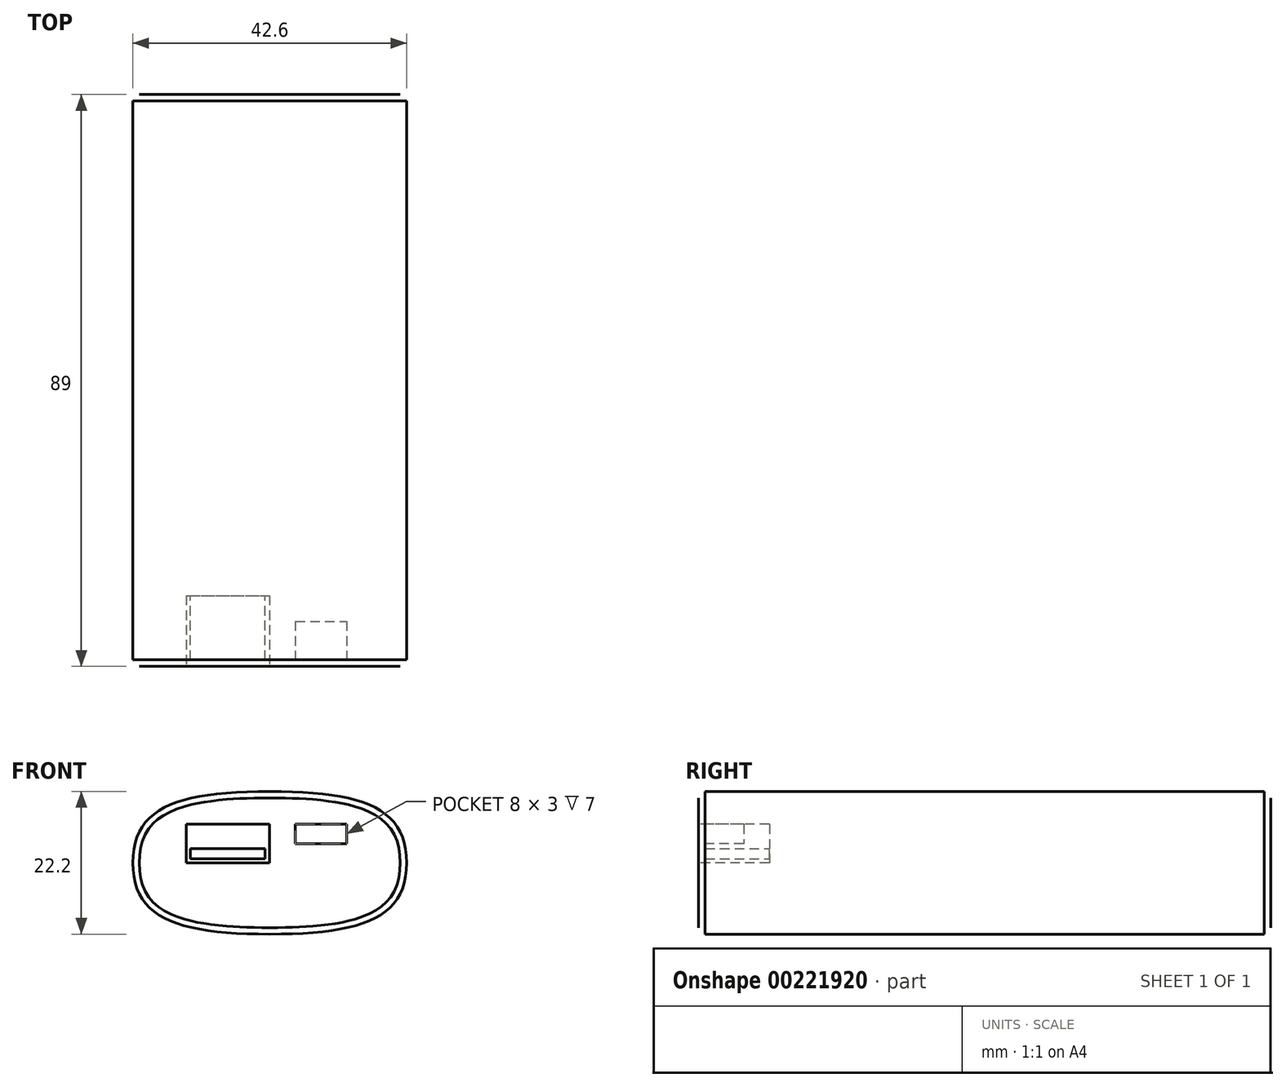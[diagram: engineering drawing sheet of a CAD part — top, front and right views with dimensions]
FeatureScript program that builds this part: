
annotation { "Feature Type Name" : "Feature", "Feature Type Description" : "" }
export const myFeature = defineFeature(function(context is Context, id is Id, definition is map)
    precondition{}
    {
        {
            var Q0;
            Q0=qCreatedBy(makeId("Front.planeOp"),FACE);
            var sketch = newSketch(context, id + "F0", { "sketchPlane" : qUnion([Q0])});
            skLineSegment(sketch, "E0", {"start": v(0, 11.1) * mm, "end": v(0, -11.1) * mm, "construction": true});
            skLineSegment(sketch, "E1", {"start": v(-21.3, 0) * mm, "end": v(21.3, 0) * mm, "construction": true});
            skFitSpline(sketch, "E2", {"points": [v(0, 11.1) * mm, v(-21.3, 0) * mm], "startDerivative": vector(-42.35, 0) * mm, "endDerivative": vector(0, -26.2) * mm});
            skFitSpline(sketch, "E3.MirrorCS", {"points": [v(0, -11.1) * mm, v(-21.3, 0) * mm], "startDerivative": vector(-42.35, 0) * mm, "endDerivative": vector(0, 26.2) * mm});
            skFitSpline(sketch, "E4.MirrorCS", {"points": [v(0, 11.1) * mm, v(21.3, 0) * mm], "startDerivative": vector(42.35, 0) * mm, "endDerivative": vector(0, -26.2) * mm});
            skFitSpline(sketch, "E5.MirrorCS", {"points": [v(0, -11.1) * mm, v(21.3, 0) * mm], "startDerivative": vector(42.35, 0) * mm, "endDerivative": vector(0, 26.2) * mm});
            skSolve(sketch);
        }
        {
            var Q0;
            Q0=makeQuery(id+"F0.imprint","IMPRINT",FACE,{"disambiguationData":[TD([[makeQuery(id+"F0.imprint","IMPRINT",EDGE,{"derivedFrom":sQuery(id+"F0.wireOp",EDGE,"E2")}),1.0]])]});
            extrude(context, id + "F1", {"entities" : qUnion([Q0]), "depth" : 89 * mm});
        }
        {
            var Q0;
            Q0=makeQuery(id+"F1.opExtrude","CAP_FACE",FACE,{"disambiguationData":[OSD([sQuery(id+"F0.wireOp",EDGE,"E2"),sQuery(id+"F0.wireOp",EDGE,"E3.MirrorCS"),sQuery(id+"F0.wireOp",EDGE,"E4.MirrorCS"),sQuery(id+"F0.wireOp",EDGE,"E5.MirrorCS")])],"isStart":false});
            var sketch = newSketch(context, id + "F2", { "sketchPlane" : qUnion([Q0])});
            skLineSegment(sketch, "E6.bottom", {"start": v(-13, 6) * mm, "end": v(0, 6) * mm});
            skLineSegment(sketch, "E6.top", {"start": v(-13, 0) * mm, "end": v(0, 0) * mm});
            skLineSegment(sketch, "E6.left", {"start": v(-13, 6) * mm, "end": v(-13, 0) * mm});
            skLineSegment(sketch, "E6.right", {"start": v(0, 6) * mm, "end": v(0, 0) * mm});
            skPoint(sketch, "E7.firstSnap0", {"position": v(-6.5, 6) * mm});
            skLineSegment(sketch, "E7.bottom", {"start": v(4, 6) * mm, "end": v(12, 6) * mm});
            skLineSegment(sketch, "E7.top", {"start": v(4, 3) * mm, "end": v(12, 3) * mm});
            skLineSegment(sketch, "E7.left", {"start": v(4, 6) * mm, "end": v(4, 3) * mm});
            skLineSegment(sketch, "E7.right", {"start": v(12, 6) * mm, "end": v(12, 3) * mm});
            skSolve(sketch);
        }
        {
            var Q0;
            Q0=makeQuery(id+"F2.imprint","IMPRINT",FACE,{"disambiguationData":[TD([[makeQuery(id+"F2.imprint","IMPRINT",EDGE,{"derivedFrom":sQuery(id+"F2.wireOp",EDGE,"E6.bottom")}),-1.0]])]});
            extrude(context, id + "F3", {"entities" : qUnion([Q0]), "operationType" : NewBodyOperationType.REMOVE, "oppositeDirection" : true, "depth" : 11 * mm});
        }
        {
            var Q0;
            Q0=makeQuery(id+"F2.imprint","IMPRINT",FACE,{"disambiguationData":[TD([[makeQuery(id+"F2.imprint","IMPRINT",EDGE,{"derivedFrom":sQuery(id+"F2.wireOp",EDGE,"E7.bottom")}),-1.0]])]});
            extrude(context, id + "F4", {"entities" : qUnion([Q0]), "operationType" : NewBodyOperationType.REMOVE, "oppositeDirection" : true, "depth" : 7 * mm});
        }
        {
            var Q0;
            Q0=makeQuery(id+"F1.opExtrude","CAP_EDGE",EDGE,{"disambiguationData":[OSD([sQuery(id+"F0.wireOp",EDGE,"E2")])],"isStart":false});
            var Q1;
            Q1=makeQuery(id+"F1.opExtrude","CAP_EDGE",EDGE,{"disambiguationData":[OSD([sQuery(id+"F0.wireOp",EDGE,"E2")])],"isStart":true});
            chamfer(context, id + "F5", {"entities" : qUnion([Q0, Q1]), "width" : 1 * mm, "tangentPropagation" : true});
        }
        {
            var Q0;
            Q0=makeQuery(id+"F3.boolean.opBoolean","COPY",FACE,{"derivedFrom":makeQuery(id+"F3.opExtrude","CAP_FACE",FACE,{"disambiguationData":[OSD([sQuery(id+"F2.wireOp",EDGE,"E6.bottom"),sQuery(id+"F2.wireOp",EDGE,"E6.top"),sQuery(id+"F2.wireOp",EDGE,"E6.left"),sQuery(id+"F2.wireOp",EDGE,"E6.right")])],"isStart":false})});
            var sketch = newSketch(context, id + "F6", { "sketchPlane" : qUnion([Q0])});
            skLineSegment(sketch, "E8.bottom", {"start": v(-12.34, 0.62) * mm, "end": v(-0.75, 0.62) * mm});
            skLineSegment(sketch, "E8.top", {"start": v(-12.34, 2.2) * mm, "end": v(-0.75, 2.2) * mm});
            skLineSegment(sketch, "E8.left", {"start": v(-12.34, 0.62) * mm, "end": v(-12.34, 2.2) * mm});
            skLineSegment(sketch, "E8.right", {"start": v(-0.75, 0.62) * mm, "end": v(-0.75, 2.2) * mm});
            skSolve(sketch);
        }
        {
            var Q0;
            Q0=makeQuery(id+"F6.imprint","IMPRINT",FACE,{"disambiguationData":[TD([[makeQuery(id+"F6.imprint","IMPRINT",EDGE,{"derivedFrom":sQuery(id+"F6.wireOp",EDGE,"E8.bottom")}),1.0]])]});
            extrude(context, id + "F7", {"entities" : qUnion([Q0]), "operationType" : NewBodyOperationType.ADD, "depth" : 10 * mm});
        }
    });
